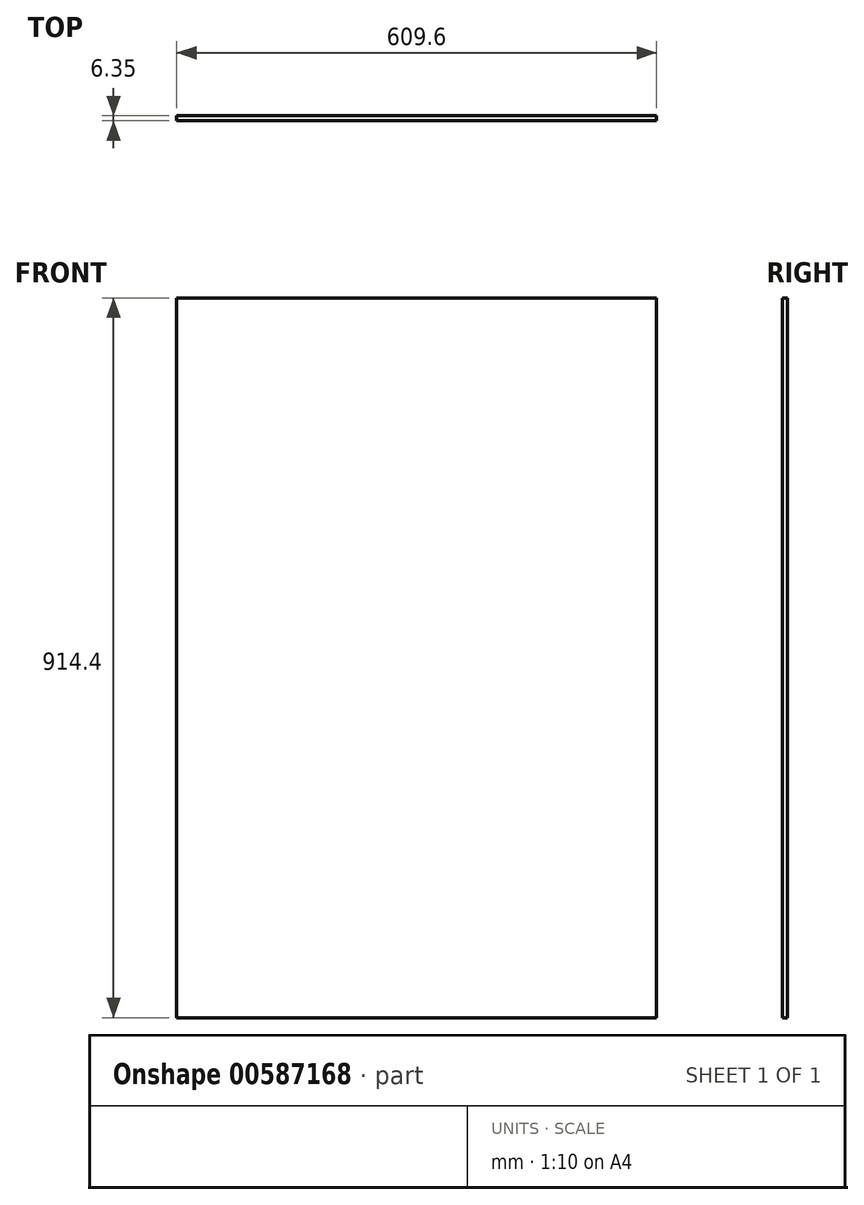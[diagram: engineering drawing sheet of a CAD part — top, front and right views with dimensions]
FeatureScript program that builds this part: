
annotation { "Feature Type Name" : "Feature", "Feature Type Description" : "" }
export const myFeature = defineFeature(function(context is Context, id is Id, definition is map)
    precondition{}
    {
        {
            var Q0;
            Q0=qCreatedBy(makeId("Front.planeOp"),FACE);
            var sketch = newSketch(context, id + "F0", { "sketchPlane" : qUnion([Q0])});
            skLineSegment(sketch, "E0.bottom", {"start": v(-304.8, 457.2) * mm, "end": v(304.8, 457.2) * mm});
            skLineSegment(sketch, "E0.top", {"start": v(-304.8, -457.2) * mm, "end": v(304.8, -457.2) * mm});
            skLineSegment(sketch, "E0.left", {"start": v(-304.8, 457.2) * mm, "end": v(-304.8, -457.2) * mm});
            skLineSegment(sketch, "E0.right", {"start": v(304.8, 457.2) * mm, "end": v(304.8, -457.2) * mm});
            skSolve(sketch);
        }
        {
            var Q0;
            Q0=qSketchRegion(id+"F0",true);
            extrude(context, id + "F1", {"entities" : qUnion([Q0]), "depth" : 6.35 * mm, "offsetDistance" : 25.4 * mm});
        }
    });
